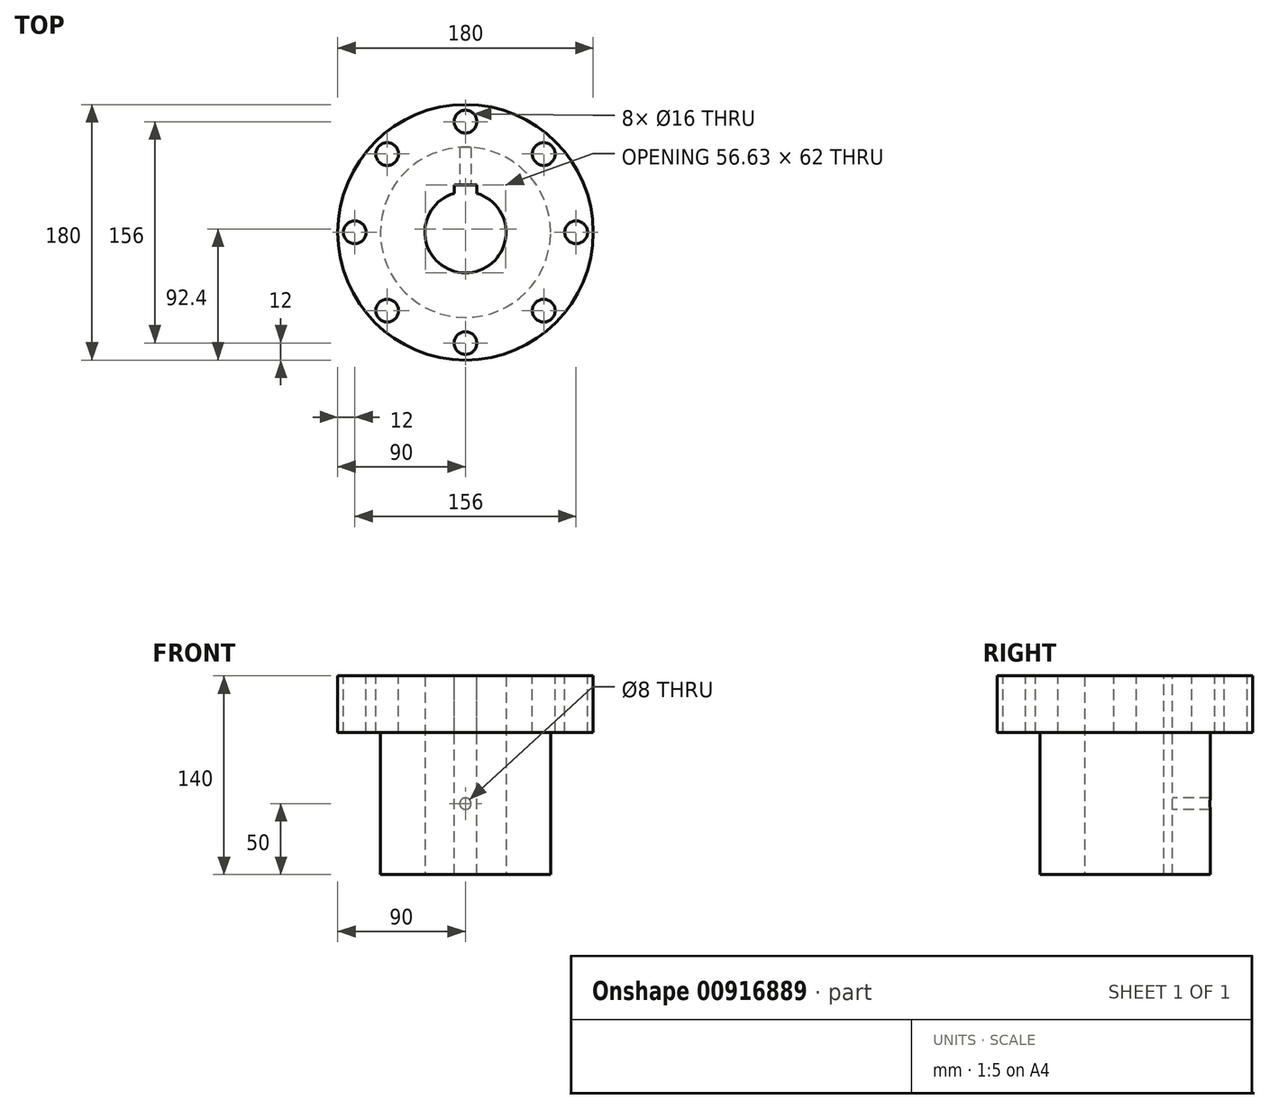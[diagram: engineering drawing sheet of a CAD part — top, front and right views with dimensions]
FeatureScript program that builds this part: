
annotation { "Feature Type Name" : "Feature", "Feature Type Description" : "" }
export const myFeature = defineFeature(function(context is Context, id is Id, definition is map)
    precondition{}
    {
        {
            var Q0;
            Q0=qCreatedBy(makeId("Front.planeOp"),FACE);
            var sketch = newSketch(context, id + "F0", { "sketchPlane" : qUnion([Q0])});
            skLineSegment(sketch, "E0", {"start": v(28.6, 0) * mm, "end": v(28.6, 140) * mm});
            skLineSegment(sketch, "E1", {"start": v(28.6, 140) * mm, "end": v(90, 140) * mm});
            skLineSegment(sketch, "E2", {"start": v(90, 140) * mm, "end": v(90, 100) * mm});
            skLineSegment(sketch, "E3", {"start": v(90, 100) * mm, "end": v(60, 100) * mm});
            skLineSegment(sketch, "E4", {"start": v(60, 100) * mm, "end": v(60, 0) * mm});
            skLineSegment(sketch, "E5", {"start": v(60, 0) * mm, "end": v(28.6, 0) * mm});
            skLineSegment(sketch, "E6", {"start": v(0, -99.5) * mm, "end": v(0, 185.4) * mm, "construction": true});
            skSolve(sketch);
        }
        {
            var Q0;
            Q0 = qSketchRegion(id + "F0", true);
            var Q1;
            Q1=sQuery(id+"F0.wireOp",EDGE,"E6");
            revolve(context, id + "F1", {"surfaceOperationType" : NewSurfaceOperationType.NEW, "entities" : qUnion([Q0]), "axis" : qUnion([Q1]), "revolveType" : RevolveType.FULL});
        }
        {
            var Q0;
            Q0=makeQuery(id+"F1.opRevolve","SWEPT_FACE",FACE,{"disambiguationData":[OSD([sQuery(id+"F0.wireOp",EDGE,"E1")])]});
            var sketch = newSketch(context, id + "F2", { "sketchPlane" : qUnion([Q0])});
            skLineSegment(sketch, "E7", {"start": v(-8, 33.4) * mm, "end": v(8, 33.4) * mm});
            skLineSegment(sketch, "E8", {"start": v(8, 33.4) * mm, "end": v(8, 27.46) * mm});
            skLineSegment(sketch, "E9", {"start": v(-8, 33.4) * mm, "end": v(-8, 27.46) * mm});
            skLineSegment(sketch, "E10", {"start": v(8, 27.46) * mm, "end": v(-8, 27.46) * mm});
            skSolve(sketch);
        }
        {
            var Q0;
            Q0=makeQuery(id+"F2.imprint","IMPRINT",FACE,{"disambiguationData":[TD([[makeQuery(id+"F2.imprint","IMPRINT",EDGE,{"derivedFrom":sQuery(id+"F2.wireOp",EDGE,"E7")}),-1.0]])]});
            extrude(context, id + "F3", {"entities" : qUnion([Q0]), "operationType" : NewBodyOperationType.REMOVE, "endBound" : BoundingType.THROUGH_ALL, "oppositeDirection" : true, "depth" : 25 * mm, "offsetDistance" : 25 * mm});
        }
        {
            var Q0;
            Q0=makeQuery(id+"F1.opRevolve","SWEPT_FACE",FACE,{"disambiguationData":[OSD([sQuery(id+"F0.wireOp",EDGE,"E1")])]});
            var sketch = newSketch(context, id + "F4", { "sketchPlane" : qUnion([Q0])});
            skCircle(sketch, "E11", {"center": v(0, 78) * mm, "radius": 8 * mm});
            skCircle(sketch, "E12.1.0", {"center": v(-55.15, 55.15) * mm, "radius": 8 * mm});
            skCircle(sketch, "E12.2.0", {"center": v(-78, 0) * mm, "radius": 8 * mm});
            skCircle(sketch, "E12.3.0", {"center": v(-55.15, -55.15) * mm, "radius": 8 * mm});
            skCircle(sketch, "E12.4.0", {"center": v(0, -78) * mm, "radius": 8 * mm});
            skCircle(sketch, "E12.5.0", {"center": v(55.15, -55.15) * mm, "radius": 8 * mm});
            skCircle(sketch, "E12.6.0", {"center": v(78, 0) * mm, "radius": 8 * mm});
            skCircle(sketch, "E12.7.0", {"center": v(55.15, 55.15) * mm, "radius": 8 * mm});
            skPoint(sketch, "E12.center", {"position": v(0, 0) * mm});
            skSolve(sketch);
        }
        {
            var Q0;
            Q0=makeQuery(id+"F4.imprint","IMPRINT",FACE,{"disambiguationData":[TD([[makeQuery(id+"F4.imprint","IMPRINT",EDGE,{"derivedFrom":sQuery(id+"F4.wireOp",EDGE,"E12.1.0")}),1.0]])]});
            var Q1;
            Q1=makeQuery(id+"F4.imprint","IMPRINT",FACE,{"disambiguationData":[TD([[makeQuery(id+"F4.imprint","IMPRINT",EDGE,{"derivedFrom":sQuery(id+"F4.wireOp",EDGE,"E11")}),1.0]])]});
            var Q2;
            Q2=makeQuery(id+"F4.imprint","IMPRINT",FACE,{"disambiguationData":[TD([[makeQuery(id+"F4.imprint","IMPRINT",EDGE,{"derivedFrom":sQuery(id+"F4.wireOp",EDGE,"E12.7.0")}),1.0]])]});
            var Q3;
            Q3=makeQuery(id+"F4.imprint","IMPRINT",FACE,{"disambiguationData":[TD([[makeQuery(id+"F4.imprint","IMPRINT",EDGE,{"derivedFrom":sQuery(id+"F4.wireOp",EDGE,"E12.6.0")}),1.0]])]});
            var Q4;
            Q4=makeQuery(id+"F4.imprint","IMPRINT",FACE,{"disambiguationData":[TD([[makeQuery(id+"F4.imprint","IMPRINT",EDGE,{"derivedFrom":sQuery(id+"F4.wireOp",EDGE,"E12.5.0")}),1.0]])]});
            var Q5;
            Q5=makeQuery(id+"F4.imprint","IMPRINT",FACE,{"disambiguationData":[TD([[makeQuery(id+"F4.imprint","IMPRINT",EDGE,{"derivedFrom":sQuery(id+"F4.wireOp",EDGE,"E12.4.0")}),1.0]])]});
            var Q6;
            Q6=makeQuery(id+"F4.imprint","IMPRINT",FACE,{"disambiguationData":[TD([[makeQuery(id+"F4.imprint","IMPRINT",EDGE,{"derivedFrom":sQuery(id+"F4.wireOp",EDGE,"E12.3.0")}),1.0]])]});
            var Q7;
            Q7=makeQuery(id+"F4.imprint","IMPRINT",FACE,{"disambiguationData":[TD([[makeQuery(id+"F4.imprint","IMPRINT",EDGE,{"derivedFrom":sQuery(id+"F4.wireOp",EDGE,"E12.2.0")}),1.0]])]});
            extrude(context, id + "F5", {"entities" : qUnion([Q0, Q1, Q2, Q3, Q4, Q5, Q6, Q7]), "operationType" : NewBodyOperationType.REMOVE, "endBound" : BoundingType.THROUGH_ALL, "oppositeDirection" : true, "depth" : 25 * mm, "offsetDistance" : 25 * mm});
        }
        {
            var Q0;
            Q0=qCreatedBy(makeId("Front.planeOp"),FACE);
            var sketch = newSketch(context, id + "F6", { "sketchPlane" : qUnion([Q0])});
            skCircle(sketch, "E13", {"center": v(0, 50) * mm, "radius": 4 * mm});
            skSolve(sketch);
        }
        {
            var Q0;
            Q0 = qSketchRegion(id + "F6", true);
            extrude(context, id + "F7", {"entities" : qUnion([Q0]), "operationType" : NewBodyOperationType.REMOVE, "endBound" : BoundingType.THROUGH_ALL, "oppositeDirection" : true, "depth" : 25 * mm, "offsetDistance" : 25 * mm});
        }
    });
